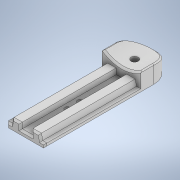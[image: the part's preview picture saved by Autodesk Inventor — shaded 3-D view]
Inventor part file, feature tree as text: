
AUTODESK INVENTOR PART (.ipt)
format: ipt  version: 2021 (Build 250183000, 183)  size: 228,864 bytes
history: native  units: mm
features: extrude x6, sketch x6, chamfer x1
ambient origin geometry x8: Origin, YZ Plane, XZ Plane, XY Plane, X Axis, Y Axis, Z Axis, Center Point
bodies: Solid1 (feature_tree)
feature tree (13):
  extrude  "Extrusion1"  Depth=108.0mm
  extrude  "Extrusion2"  Depth=6.0mm
  extrude  "Extrusion3"  Depth=21.75mm
  extrude  "Extrusion4"  Depth=47.0mm
  extrude  "Extrusion11"  Depth=12.0mm
  extrude  "Extrusion12"  Depth=6.5mm
  chamfer  "Chamfer2"  Distance=9.5mm
  sketch  "Sketch1"  dims[d0=43.5mm d1=108.0mm]
  sketch  "Sketch2"  dims[d2=6.0mm d3=6.0mm]
  sketch  "Sketch3"  dims[d4=21.75mm d5=21.75mm]
  sketch  "Sketch4"  dims[d6=47.0mm d7=47.0mm]
  sketch  "Sketch12"  dims[d8=5.0mm d9=0.0mm d10=12.0mm]
  sketch  "Sketch13"  dims[d11=6.0mm d12=9.5mm d13=9.5mm d14=6.5mm d15=0.0mm d16=1.5mm d17=1.5mm d18=6.5mm d19=0.0mm d20=15.0mm d21=15.5mm d22=0.0mm d48=36.5mm d49=1.0mm d50=0.0mm d51=8.1mm d52=1.0mm d53=0.0mm d54=2.0mm d55=2.0mm d56=45.0deg d39=0.5mm d40=0.872665mm d41=0.5mm d42=0.872665mm d43=0.5mm d44=0.872665mm d45=0.5mm d46=0.872665mm]
